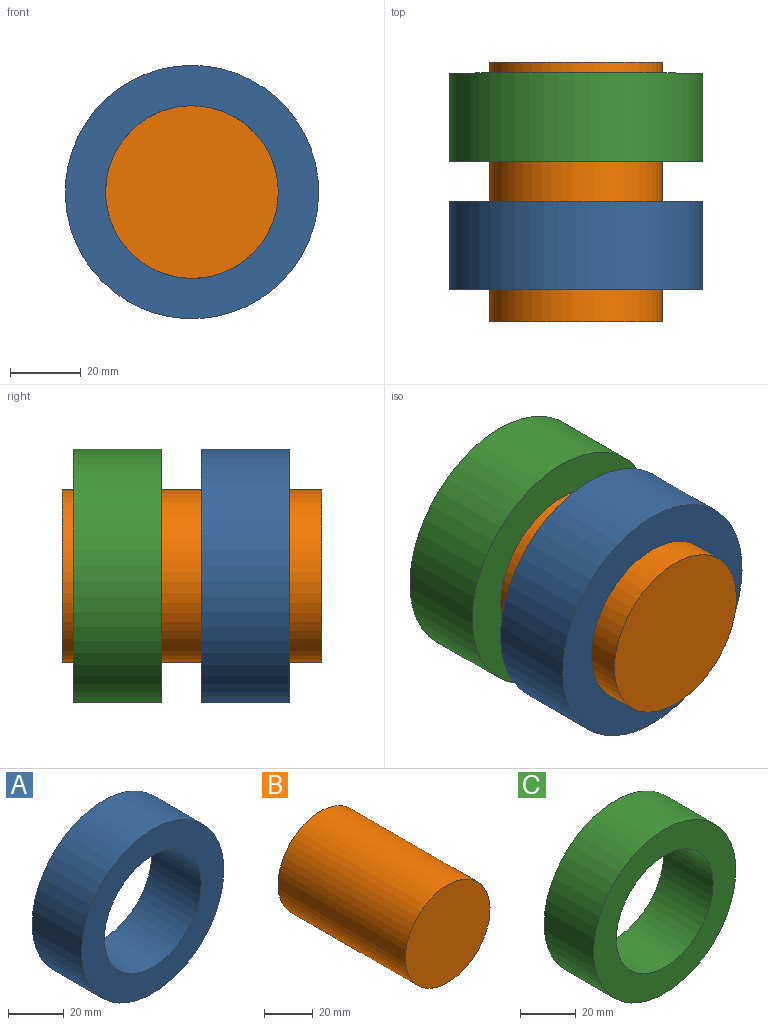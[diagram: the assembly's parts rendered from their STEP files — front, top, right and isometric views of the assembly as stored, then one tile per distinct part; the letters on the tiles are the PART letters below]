
ASSEMBLY  parts=3 mates=2
PART A: 4 faces, bbox 71.9x25x71.9 mm
  f0: cylinder r=24.48mm len=48.96mm, axis (0,1,0), area 3844.9mm2, adj f2,f3
  f1: cylinder r=35.94mm len=71.88mm, axis (0,1,0), area 5645.7mm2, adj f2,f3
  f2: plane 71.88x71.88mm, normal (0,-1,0), area 2176mm2, adj f0,f1
  f3: plane 71.88x71.88mm, normal (0,1,0), area 2176mm2, adj f0,f1
PART B: 3 faces, bbox 49x73.7x49 mm
  f0: cylinder r=24.48mm len=73.66mm, axis (0,1,0), area 11328.7mm2, adj f1,f2
  f1: plane 48.96x48.96mm, normal (0,-1,0), area 1882.3mm2, adj f0
  f2: plane 48.96x48.96mm, normal (0,1,0), area 1882.3mm2, adj f0
PART C: 4 faces, bbox 71.9x25x71.9 mm
  f0: cylinder r=24.48mm len=48.96mm, axis (0,1,0), area 3844.9mm2, adj f2,f3
  f1: cylinder r=35.94mm len=71.88mm, axis (0,1,0), area 5645.7mm2, adj f2,f3
  f2: plane 71.88x71.88mm, normal (0,-1,0), area 2176mm2, adj f0,f1
  f3: plane 71.88x71.88mm, normal (0,1,0), area 2176mm2, adj f0,f1
PLACE A rot(axis=(0,1,0),10deg) t=(-26.81,48.21,54.16)mm
PLACE B rot(axis=(0,1,0),100deg) t=(-26.81,14.01,54.16)mm
PLACE C rot(axis=(0,1,0),10deg) t=(-26.81,17.56,54.16)mm
MATE slider A.f1 <-> B.f0  axis (0,1,0) through (-26.81,-37.95,54.16)mm
MATE slider C.f0 <-> B.f0  axis (0,1,0) through (-26.81,-14.1,54.16)mm
